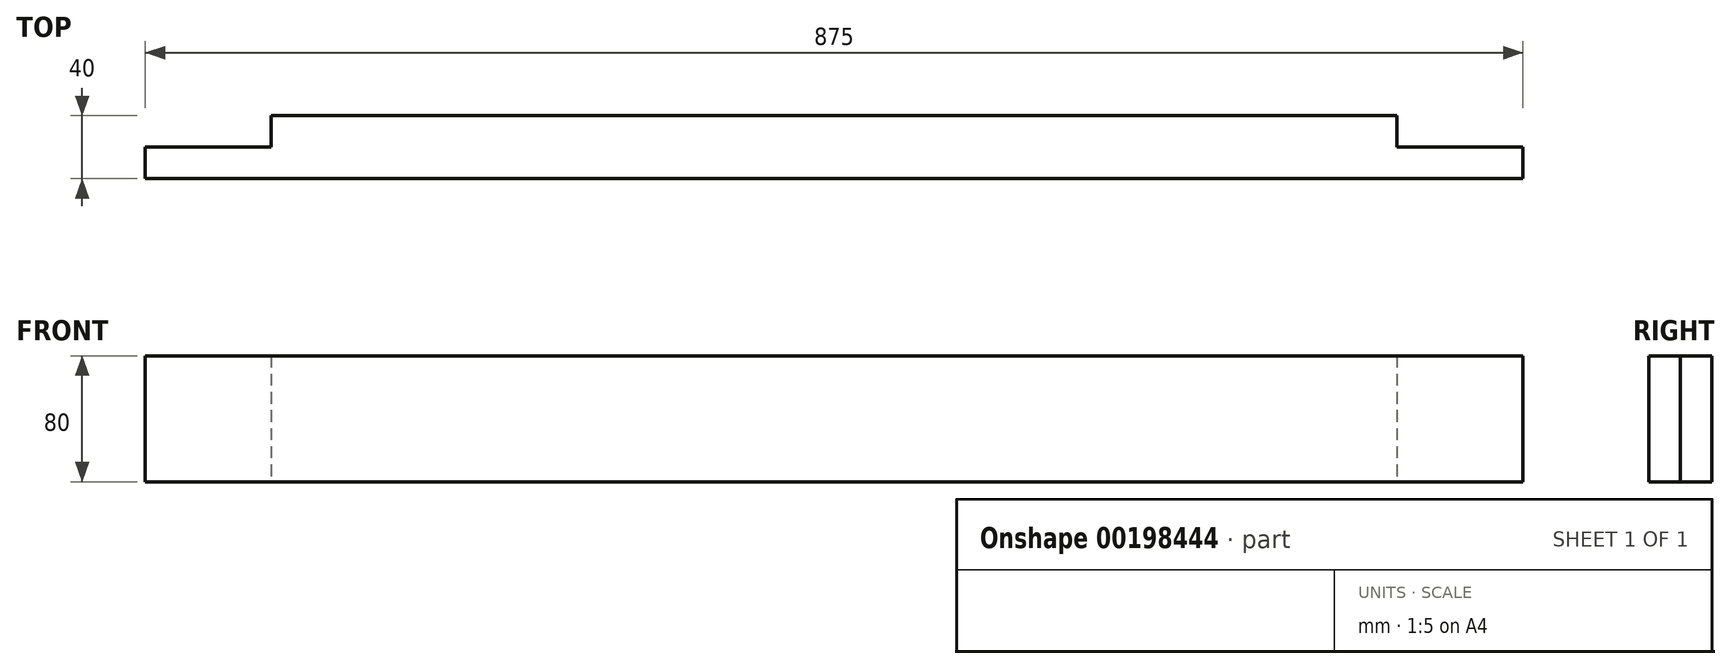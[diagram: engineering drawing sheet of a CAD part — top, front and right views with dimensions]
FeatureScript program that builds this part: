
annotation { "Feature Type Name" : "Feature", "Feature Type Description" : "" }
export const myFeature = defineFeature(function(context is Context, id is Id, definition is map)
    precondition{}
    {
        {
            var Q0;
            Q0=qCreatedBy(makeId("Top.planeOp"),FACE);
            var sketch = newSketch(context, id + "F0", { "sketchPlane" : qUnion([Q0])});
            skLineSegment(sketch, "E0.bottom", {"start": v(0, 0) * mm, "end": v(875, 0) * mm});
            skLineSegment(sketch, "E0.top", {"start": v(80, 40) * mm, "end": v(795, 40) * mm});
            skLineSegment(sketch, "E0.left", {"start": v(0, 0) * mm, "end": v(0, 20) * mm});
            skLineSegment(sketch, "E0.right", {"start": v(875, 0) * mm, "end": v(875, 20) * mm});
            skLineSegment(sketch, "E1.top", {"start": v(0, 20) * mm, "end": v(80, 20) * mm});
            skLineSegment(sketch, "E1.right", {"start": v(80, 40) * mm, "end": v(80, 20) * mm});
            skLineSegment(sketch, "E2.top", {"start": v(875, 20) * mm, "end": v(795, 20) * mm});
            skLineSegment(sketch, "E2.right", {"start": v(795, 40) * mm, "end": v(795, 20) * mm});
            skSolve(sketch);
        }
        {
            var Q0;
            Q0=makeQuery(id+"F0.imprint","IMPRINT",FACE,{"disambiguationData":[TD([[makeQuery(id+"F0.imprint","IMPRINT",EDGE,{"derivedFrom":sQuery(id+"F0.wireOp",EDGE,"E0.bottom")}),1.0]])]});
            extrude(context, id + "F1", {"entities" : qUnion([Q0]), "depth" : 80 * mm});
        }
    });
